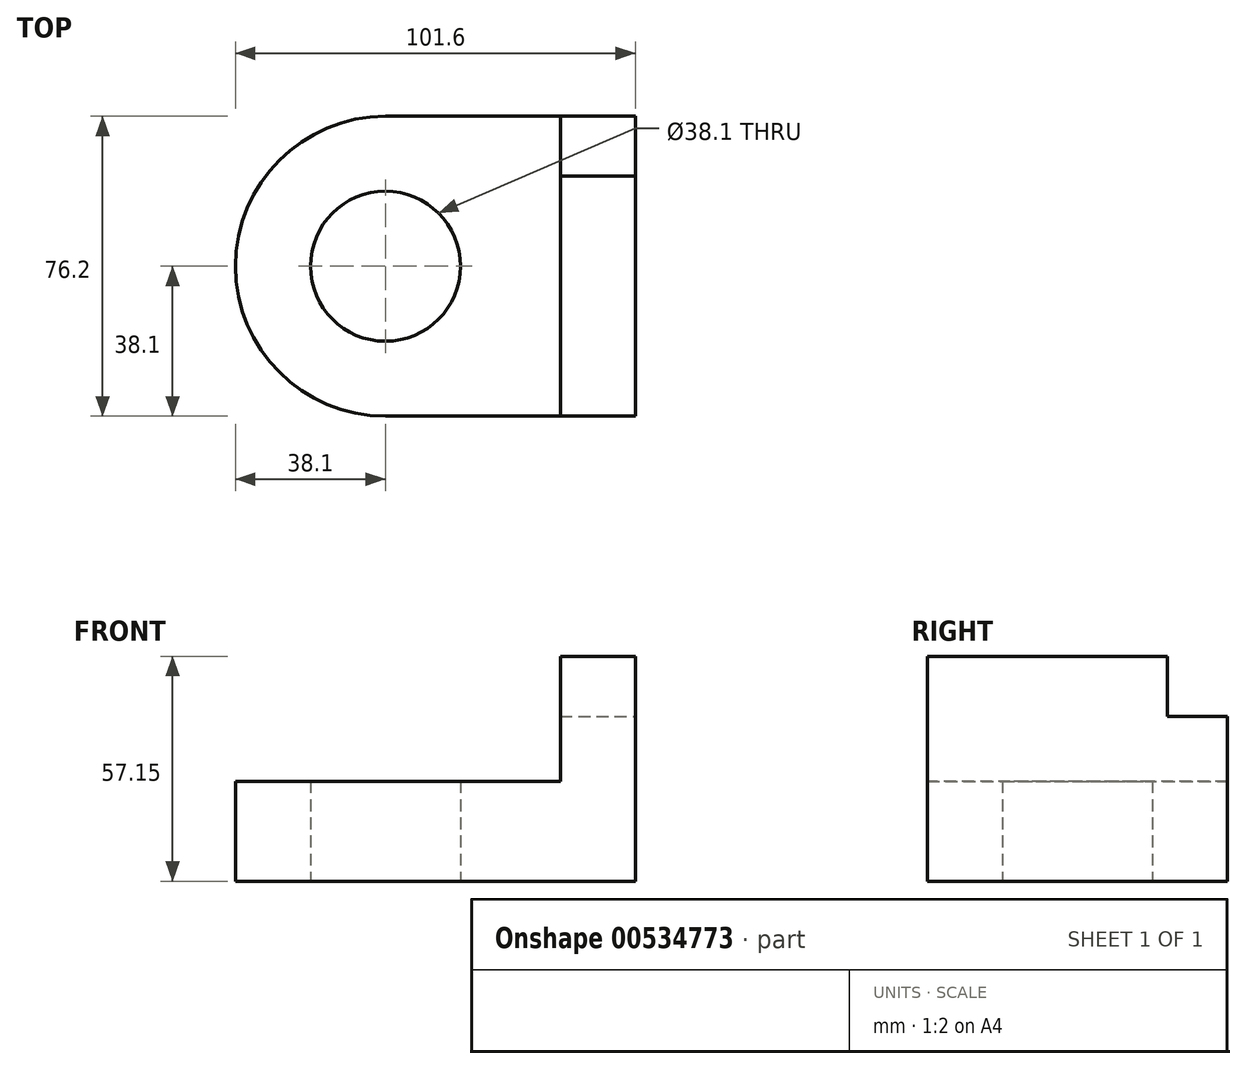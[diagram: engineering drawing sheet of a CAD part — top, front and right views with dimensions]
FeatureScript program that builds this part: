
annotation { "Feature Type Name" : "Feature", "Feature Type Description" : "" }
export const myFeature = defineFeature(function(context is Context, id is Id, definition is map)
    precondition{}
    {
        {
            var Q0;
            Q0=qCreatedBy(makeId("Top.planeOp"),FACE);
            var sketch = newSketch(context, id + "F0", { "sketchPlane" : qUnion([Q0])});
            skArc(sketch, "E0", {"start": v(0, 38.1) * mm, "mid": v(-38.1, 0) * mm, "end": v(0, -38.1) * mm});
            skLineSegment(sketch, "E1.bottom", {"start": v(0, -38.1) * mm, "end": v(63.5, -38.1) * mm});
            skLineSegment(sketch, "E1.top", {"start": v(0, 38.1) * mm, "end": v(63.5, 38.1) * mm});
            skLineSegment(sketch, "E1.right", {"start": v(63.5, -38.1) * mm, "end": v(63.5, 38.1) * mm});
            skCircle(sketch, "E2", {"center": v(0, 0) * mm, "radius": 19.05 * mm});
            skSolve(sketch);
        }
        {
            var Q0;
            Q0=makeQuery(id+"F0.imprint","IMPRINT",FACE,{"disambiguationData":[TD([[makeQuery(id+"F0.imprint","IMPRINT",EDGE,{"derivedFrom":sQuery(id+"F0.wireOp",EDGE,"E0")}),1.0]])]});
            extrude(context, id + "F1", {"entities" : qUnion([Q0]), "depth" : 25.4 * mm, "offsetDistance" : 25.4 * mm});
        }
        {
            var Q0;
            Q0=makeQuery(id+"F1.opExtrude","SWEPT_FACE",FACE,{"disambiguationData":[OSD([sQuery(id+"F0.wireOp",EDGE,"E1.right")])]});
            var sketch = newSketch(context, id + "F2", { "sketchPlane" : qUnion([Q0])});
            skLineSegment(sketch, "E3.bottom", {"start": v(-38.1, 25.4) * mm, "end": v(38.1, 25.4) * mm});
            skLineSegment(sketch, "E3.top", {"start": v(-38.1, 57.15) * mm, "end": v(22.86, 57.15) * mm});
            skLineSegment(sketch, "E3.left", {"start": v(-38.1, 25.4) * mm, "end": v(-38.1, 57.15) * mm});
            skLineSegment(sketch, "E3.right", {"start": v(38.1, 25.4) * mm, "end": v(38.1, 41.91) * mm});
            skLineSegment(sketch, "E4.top", {"start": v(38.1, 41.91) * mm, "end": v(22.86, 41.91) * mm});
            skLineSegment(sketch, "E4.right", {"start": v(22.86, 57.15) * mm, "end": v(22.86, 41.91) * mm});
            skPoint(sketch, "E5.orphan", {"position": v(38.1, 57.15) * mm});
            skSolve(sketch);
        }
        {
            var Q0;
            Q0=makeQuery(id+"F2.imprint","IMPRINT",FACE,{"disambiguationData":[TD([[makeQuery(id+"F2.imprint","IMPRINT",EDGE,{"derivedFrom":sQuery(id+"F2.wireOp",EDGE,"E3.bottom")}),1.0]])]});
            extrude(context, id + "F3", {"entities" : qUnion([Q0]), "operationType" : NewBodyOperationType.ADD, "oppositeDirection" : true, "depth" : 19.05 * mm, "offsetDistance" : 25.4 * mm});
        }
    });
